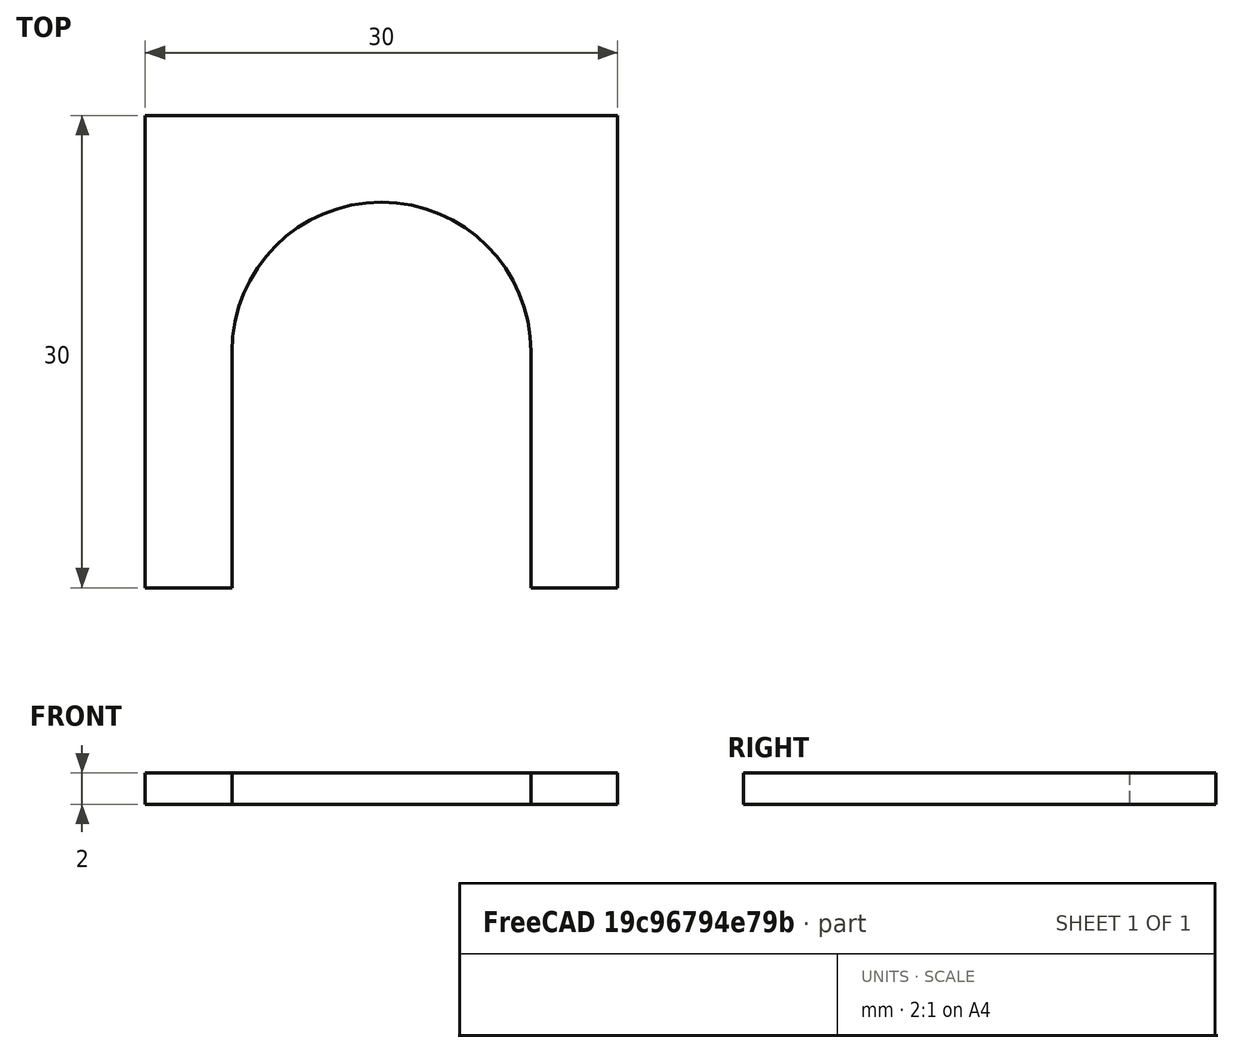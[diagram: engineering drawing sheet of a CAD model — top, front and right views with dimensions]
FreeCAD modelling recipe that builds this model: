
FCSTD DOCUMENT  (FreeCAD 0.20R29177 +426 (Git))
Label: Cable clamp washer
License: All rights reserved
LicenseURL: http://en.wikipedia.org/wiki/All_rights_reserved
objects: Sketcher::SketchObject×1, PartDesign::Pad×1, PartDesign::Body×1
note: 4 computed .brp shape members not serialized (recipe doc carries the construction recipe); baked Part::Feature solids carry a one-line shape summary decoded from their .brp

FEATURE [Sketcher::SketchObject] Sketch
  FullyConstrained = true
  MapMode = 5
  Support = -> [XY_Plane]
  sketch-geometry (8):
    g0: LineSegment StartX=-9.5 StartY=8e-16 StartZ=0 EndX=-9.5 EndY=-15 EndZ=0
    g1: LineSegment StartX=-9.5 StartY=-15 StartZ=0 EndX=-15 EndY=-15 EndZ=0
    g2: LineSegment StartX=-15 StartY=-15 StartZ=0 EndX=-15 EndY=15 EndZ=0
    g3: LineSegment StartX=-15 StartY=15 StartZ=0 EndX=15 EndY=15 EndZ=0
    g4: LineSegment StartX=15 StartY=15 StartZ=0 EndX=15 EndY=-15 EndZ=0
    g5: LineSegment StartX=15 StartY=-15 StartZ=0 EndX=9.5 EndY=-15 EndZ=0
    g6: LineSegment StartX=9.5 StartY=-15 StartZ=0 EndX=9.5 EndY=0 EndZ=0
    g7: ArcOfCircle CenterX=4e-16 CenterY=-8.04283e-08 CenterZ=0 NormalX=0 NormalY=0 NormalZ=1 AngleXU=0 Radius=9.5 StartAngle=8.46614e-09 EndAngle=3.14159
  constraints (22):
    c: Vertical(g0)
    c: Coincident(g0,g1)
    c: Horizontal(g1)
    c: Coincident(g2,g3)
    c: Coincident(g3,g4)
    c: Vertical(g4)
    c: Coincident(g4,g5)
    c: Horizontal(g5)
    c: Coincident(g5,g6)
    c: Vertical(g6)
    c: DistanceX(g0,g5) = 19
    c: Symmetric(g0,g5,g-2)
    c: Horizontal(g0,g6)
    c: DistanceY(g6,g6) = 15
    c: Coincident(g7,g0)
    c: Coincident(g7,g6)
    c: DistanceY(g2,g2) = 30
    c: Coincident(g1,g2)
    c: Diameter(g7) = 19
    c: Symmetric(g2,g1,g-1)
    c: Symmetric(g2,g3,g-2)
    c: DistanceX(g3,g3) = 30
FEATURE [PartDesign::Pad] Pad
  Direction = (0,0,1)
  Length = 2
  Length2 = 10
  Profile = -> Sketch
  ReferenceAxis = -> Sketch [N_Axis]
  Type = 0
FEATURE [PartDesign::Body] Body
  Group = -> [Sketch,Pad]
  Origin = -> Origin
  Tip = -> Pad
